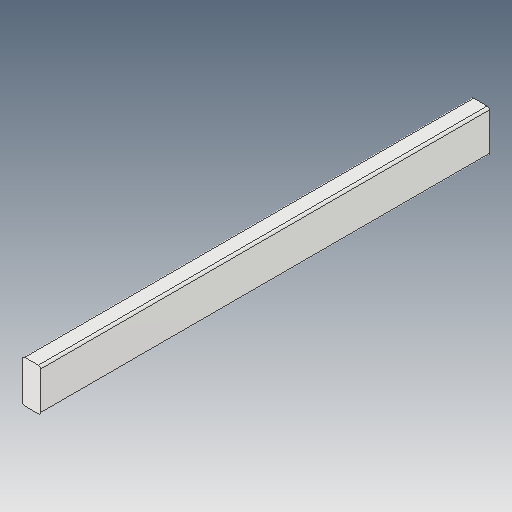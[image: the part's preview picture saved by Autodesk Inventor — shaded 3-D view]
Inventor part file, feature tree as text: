
AUTODESK INVENTOR PART (.ipt)
format: ipt  version: 2023.5 (Build 275446000, 446)  size: 86,528 bytes
history: native  units: in
note: dims shown in document units (in); Inventor stores cm internally (conversion verified against a paired STEP export)
features: fillet x1
ambient origin geometry x8: Origin, YZ Plane, XZ Plane, XY Plane, X Axis, Y Axis, Z Axis, Center Point
bodies: Solid1 (feature_tree)
feature tree (1):
  fillet  "Fillet1"  [1 undecoded]
note: 1 required parameter value undecoded (feature->parameter linkage not recoverable at this tier; creation-order binding heuristic only, values carry confidence <= 0.55)
